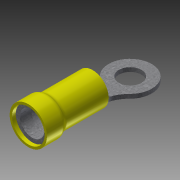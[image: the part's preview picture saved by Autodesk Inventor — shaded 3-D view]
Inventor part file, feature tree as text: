
AUTODESK INVENTOR PART (.ipt)
format: ipt  version: 2014 (Build 180170000, 170)  size: 420,352 bytes
history: native  units: in
note: dims shown in document units (in); Inventor stores cm internally (conversion verified against a paired STEP export)
features: sketch x6, fillet x5, extrude x4, projected_geometry x4, shell x1, revolve x1, plane x1, loft x1, chamfer x1, other x1
ambient origin geometry x8: Origin, YZ Plane, XZ Plane, XY Plane, X Axis, Y Axis, Z Axis, Center Point
bodies: Solid1 (feature_tree), Solid2 (feature_tree)
feature tree (25):
  extrude  "Extrusion1"  Depth=0.5595in TaperAngle=0.0deg
  extrude  "Extrusion2"  Depth=0.157in TaperAngle=0.0deg
  fillet  "Fillet1"  Radius=0.05in
  shell  "Shell1"  Thickness=0.02in
  revolve  "Revolution1"  [1 undecoded]
  plane  "Work Plane1"
  extrude  "Extrusion3"  [1 undecoded]
  loft  "Loft1"
  fillet  "Fillet2"  Radius=0.327in
  fillet  "Fillet3"  Radius=0.087in
  fillet  "Fillet4"  Radius=0.036in
  fillet  "Fillet5"  [1 undecoded]
  chamfer  "Chamfer1"  Angle=90.0deg  [1 undecoded]
  extrude  "Extrusion4"  Depth=0.036in
  sketch  "Sketch1"  dims[d0=0.2785in d1=0.5595in d2=0.0in]
  sketch  "Sketch2"  dims[d3=0.324in d4=0.157in d5=0.0in d6=0.05in d7=0.02in]
  projected_geometry  "Projected Loop1"
  sketch  "Sketch3"  dims[d9=0.035in d10=0.035in]
  sketch  "Sketch4"  dims[d11=90.0deg d12=-0.108in]
  sketch  "Sketch5"  dims[d13=0.3745in d14=0.089in d15=0.327in d16=0.087in d17=0.036in d18=0.0in d19=0.0in d20=90.0deg d21=0.0in d22=90.0deg]
  projected_geometry  "Projected Loop2"
  other  "Edges1"
  sketch  "Sketch6"  dims[d23=0.04in d24=0.04in d25=0.04in d26=0.04in d27=0.003in d28=0.125in d29=45.0deg d30=0.005in d31=0.036in d32=0.0in]
  projected_geometry  "Project Cut Edges1"
  projected_geometry  "Project Cut Edges2"
note: 4 required parameter values undecoded (feature->parameter linkage not recoverable at this tier; creation-order binding heuristic only, values carry confidence <= 0.55)